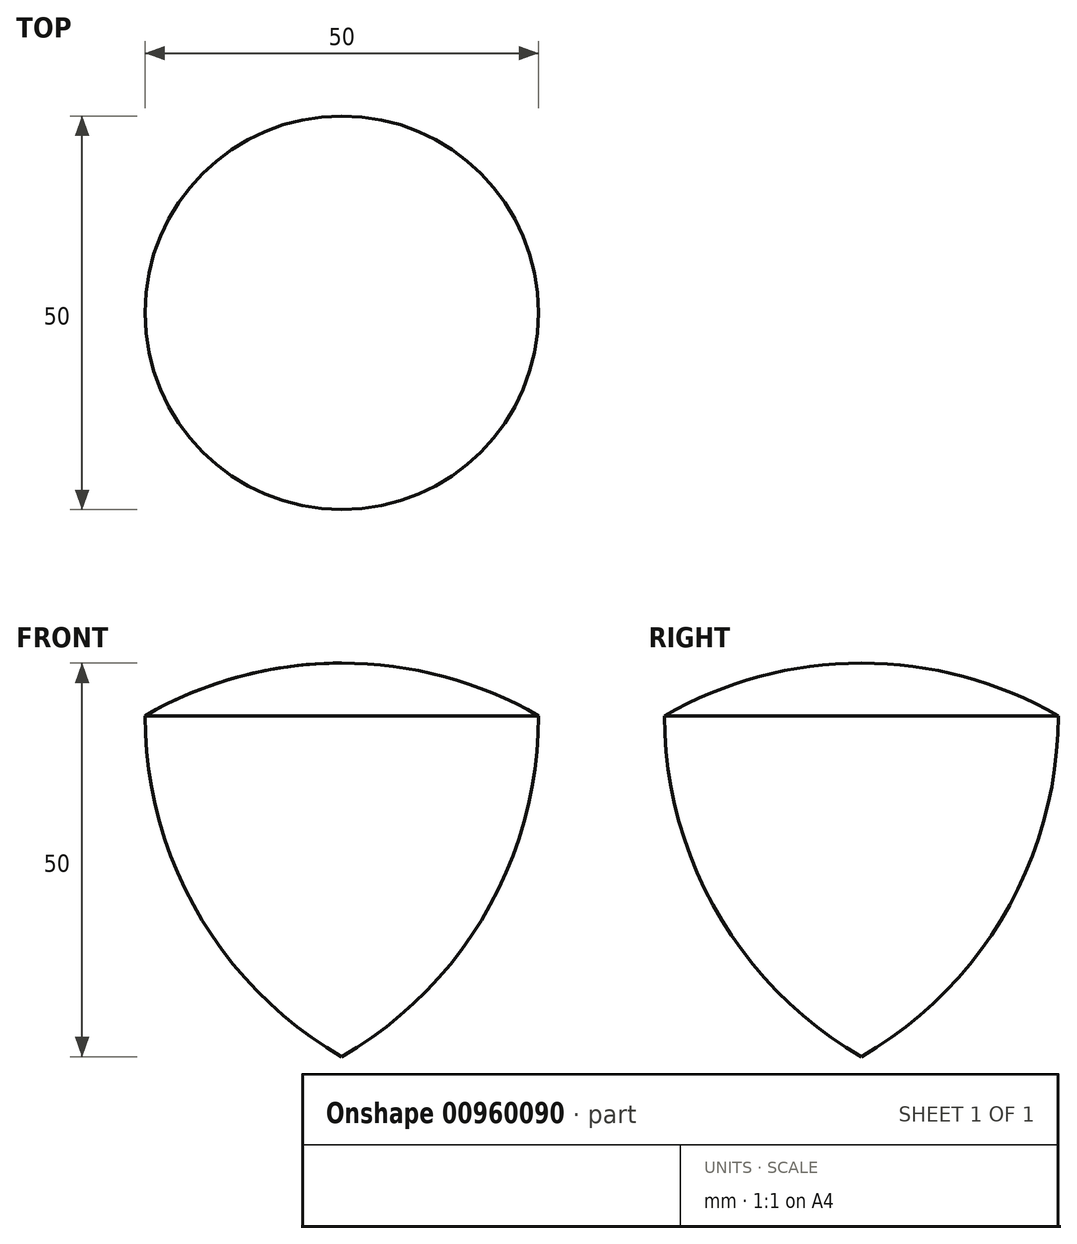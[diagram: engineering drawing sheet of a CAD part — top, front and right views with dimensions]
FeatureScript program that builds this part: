
annotation { "Feature Type Name" : "Feature", "Feature Type Description" : "" }
export const myFeature = defineFeature(function(context is Context, id is Id, definition is map)
    precondition{}
    {
        {
            var Q0;
            Q0=qCreatedBy(makeId("Front.planeOp"),FACE);
            var sketch = newSketch(context, id + "F0", { "sketchPlane" : qUnion([Q0])});
            skCircle(sketch, "E0.cCircle", {"center": v(0, 0) * mm, "radius": 14.43 * mm, "construction": true});
            skLineSegment(sketch, "E0.0", {"start": v(-25, 14.43) * mm, "end": v(25, 14.43) * mm});
            skLineSegment(sketch, "E0.1", {"start": v(25, 14.43) * mm, "end": v(0, -28.87) * mm});
            skLineSegment(sketch, "E0.2", {"start": v(0, -28.87) * mm, "end": v(-25, 14.43) * mm});
            skPoint(sketch, "E0.0.midPoint", {"position": v(0, 14.43) * mm});
            skArc(sketch, "E1", {"start": v(25, 14.43) * mm, "mid": v(0, 21.13) * mm, "end": v(-25, 14.43) * mm});
            skArc(sketch, "E2", {"start": v(-25, 14.43) * mm, "mid": v(-18.3, -10.57) * mm, "end": v(0, -28.87) * mm});
            skArc(sketch, "E3.trimOffspring", {"start": v(0, -28.87) * mm, "mid": v(18.3, -10.57) * mm, "end": v(25, 14.43) * mm});
            skLineSegment(sketch, "E4", {"start": v(0, -28.87) * mm, "end": v(0, 21.13) * mm});
            skSolve(sketch);
        }
        {
            var Q0;
            {var subQ1=sQuery(id+"F0.wireOp",EDGE,"E0.2");Q0=makeQuery(id+"F0.imprint","IMPRINT",FACE,{"disambiguationData":[TD([[makeQuery(id+"F0.imprint","IMPRINT",EDGE,{"derivedFrom":subQ1}),-1.0]])]});}
            var Q1;
            Q1=makeQuery(id+"F0.imprint","IMPRINT",FACE,{"disambiguationData":[TD([[makeQuery(id+"F0.imprint","IMPRINT",EDGE,{"derivedFrom":sQuery(id+"F0.wireOp",EDGE,"E0.2")}),1.0]])]});
            var Q2;
            {var subQ0=sQuery(id+"F0.wireOp",EDGE,"E1");var subQ3=sQuery(id+"F0.wireOp",EDGE,"E4");var subQ5=makeQuery(id+"F0.imprint","INTERSECT",VERTEX,{"derivedFrom":[subQ0,subQ3]});Q2=makeQuery(id+"F0.imprint","IMPRINT",FACE,{"disambiguationData":[TD([[makeQuery(id+"F0.imprint","IMPRINT",EDGE,{"disambiguationData":[TD([[subQ5,1.0]])],"derivedFrom":subQ3}),1.0]])]});}
            var Q3;
            Q3=sQuery(id+"F0.wireOp",EDGE,"E4");
            revolve(context, id + "F1", {"surfaceOperationType" : NewSurfaceOperationType.NEW, "entities" : qUnion([Q0, Q1, Q2]), "axis" : qUnion([Q3]), "revolveType" : RevolveType.FULL});
        }
    });
